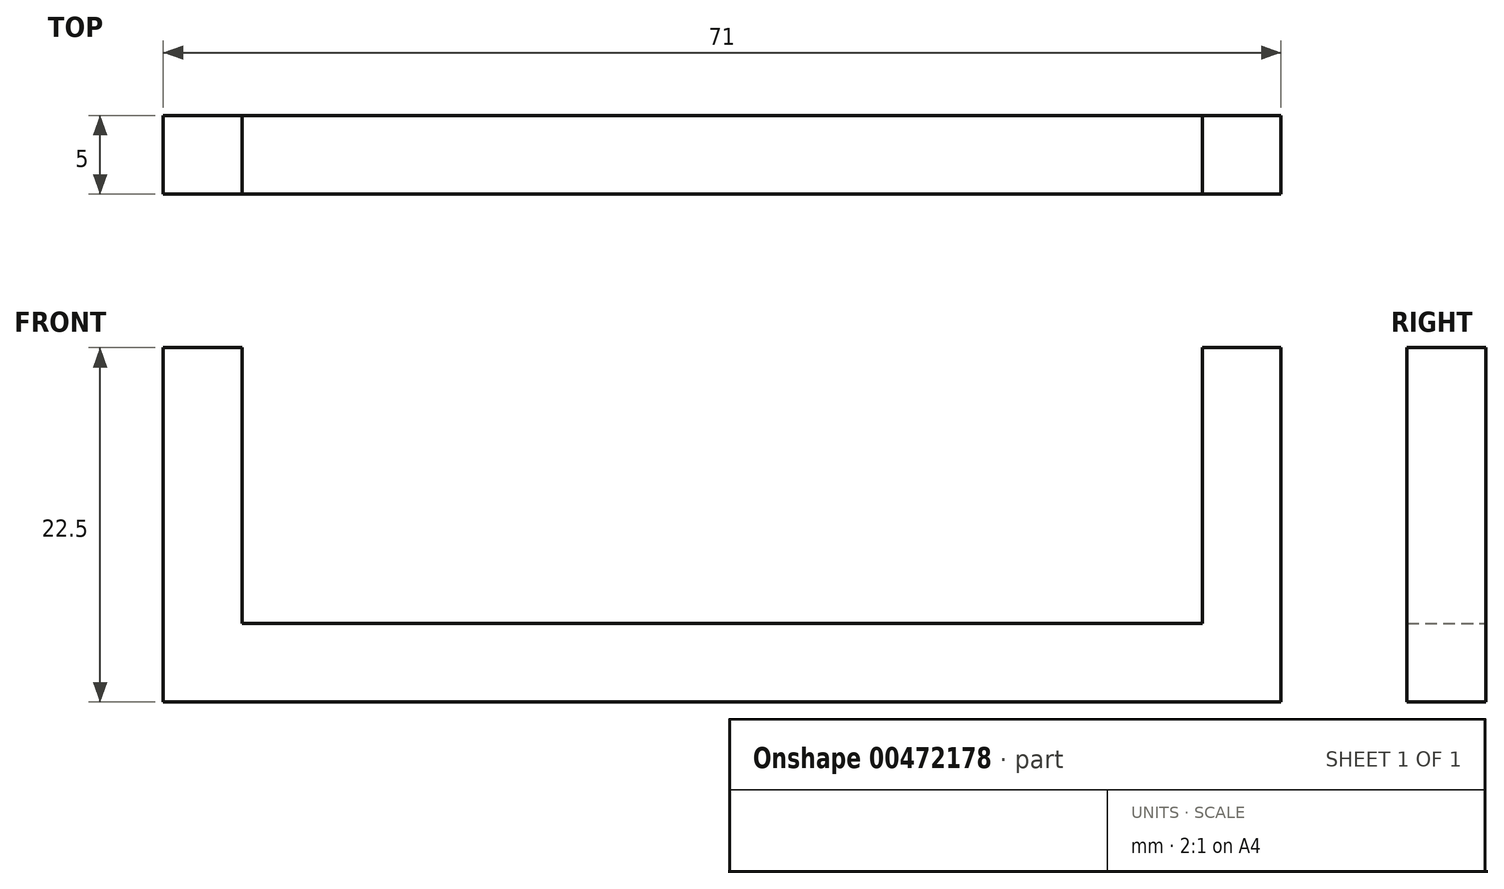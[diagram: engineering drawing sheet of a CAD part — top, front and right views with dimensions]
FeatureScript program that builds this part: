
annotation { "Feature Type Name" : "Feature", "Feature Type Description" : "" }
export const myFeature = defineFeature(function(context is Context, id is Id, definition is map)
    precondition{}
    {
        {
            var Q0;
            Q0=qCreatedBy(makeId("Front.planeOp"),FACE);
            var sketch = newSketch(context, id + "F0", { "sketchPlane" : qUnion([Q0])});
            skLineSegment(sketch, "E0", {"start": v(-33, 10) * mm, "end": v(-33, -10) * mm});
            skLineSegment(sketch, "E1", {"start": v(-33, -10) * mm, "end": v(33, -10) * mm});
            skLineSegment(sketch, "E2", {"start": v(33, -10) * mm, "end": v(33, 10) * mm});
            skSolve(sketch);
        }
        {
            var Q0;
            Q0=qCreatedBy(makeId("Top.planeOp"),FACE);
            var Q1;
            Q1=sQuery(id+"F0.wireOp",VERTEX,"E0.start");
            cPlane(context, id + "F1", {"entities" : qUnion([Q0, Q1]), "cplaneType" : CPlaneType.PLANE_POINT, "offset" : 25 * mm, "width" : 150 * mm, "height" : 150 * mm});
        }
        {
            var Q0;
            Q0=qCreatedBy(id+"F1.planeOp",FACE);
            var sketch = newSketch(context, id + "F2", { "sketchPlane" : qUnion([Q0])});
            skLineSegment(sketch, "E3.bottom", {"start": v(-35.5, 2.5) * mm, "end": v(-30.5, 2.5) * mm});
            skLineSegment(sketch, "E3.top", {"start": v(-35.5, -2.5) * mm, "end": v(-30.5, -2.5) * mm});
            skLineSegment(sketch, "E3.left", {"start": v(-35.5, 2.5) * mm, "end": v(-35.5, -2.5) * mm});
            skLineSegment(sketch, "E3.right", {"start": v(-30.5, 2.5) * mm, "end": v(-30.5, -2.5) * mm});
            skSolve(sketch);
        }
        {
            var Q0;
            Q0 = qSketchRegion(id + "F2", true);
            var Q1;
            Q1 = qConstructionFilter(qBodyType(qCreatedBy(id + "F0" ,EDGE), BodyType.WIRE), ConstructionObject.NO);
            sweep(context, id + "F3", {"profiles" : qUnion([Q0]), "path" : qUnion([Q1])});
        }
    });
